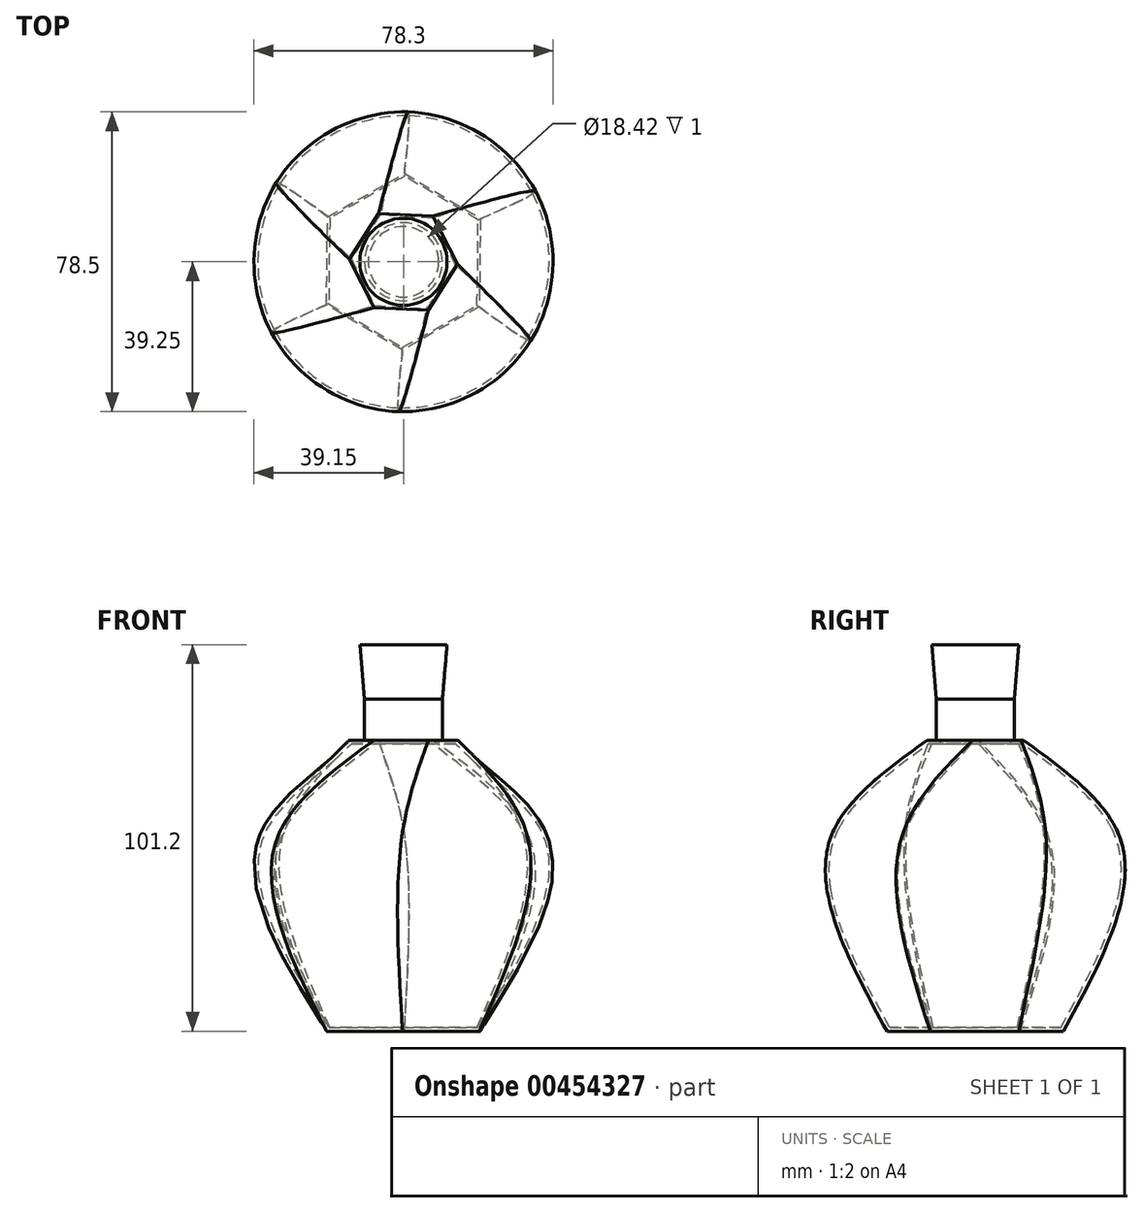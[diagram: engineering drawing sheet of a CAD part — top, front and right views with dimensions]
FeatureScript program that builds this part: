
annotation { "Feature Type Name" : "Feature", "Feature Type Description" : "" }
export const myFeature = defineFeature(function(context is Context, id is Id, definition is map)
    precondition{}
    {
        {
            var Q0;
            Q0=qCreatedBy(makeId("Top.planeOp"),FACE);
            var sketch = newSketch(context, id + "F0", { "sketchPlane" : qUnion([Q0])});
            skCircle(sketch, "E0.cCircle", {"center": v(0, 0) * mm, "radius": 23.1 * mm, "construction": true});
            skLineSegment(sketch, "E0.0", {"start": v(-20.14, -11.32) * mm, "end": v(-19.88, 11.78) * mm});
            skLineSegment(sketch, "E0.1", {"start": v(-19.88, 11.78) * mm, "end": v(0.27, 23.1) * mm});
            skLineSegment(sketch, "E0.2", {"start": v(0.27, 23.1) * mm, "end": v(20.14, 11.32) * mm});
            skLineSegment(sketch, "E0.3", {"start": v(20.14, 11.32) * mm, "end": v(19.88, -11.78) * mm});
            skLineSegment(sketch, "E0.4", {"start": v(19.88, -11.78) * mm, "end": v(-0.27, -23.1) * mm});
            skLineSegment(sketch, "E0.5", {"start": v(-0.27, -23.1) * mm, "end": v(-20.14, -11.32) * mm});
            skSolve(sketch);
        }
        {
            var Q0;
            Q0=qCreatedBy(makeId("Top.planeOp"),FACE);
            cPlane(context, id + "F1", {"entities" : qUnion([Q0]), "cplaneType" : CPlaneType.OFFSET, "offset" : 50.8 * mm, "width" : 152.4 * mm, "height" : 152.4 * mm});
        }
        {
            var Q0;
            Q0=qCreatedBy(id+"F1.planeOp",FACE);
            var sketch = newSketch(context, id + "F2", { "sketchPlane" : qUnion([Q0])});
            skCircle(sketch, "E1", {"center": v(0, 0) * mm, "radius": 37.82 * mm});
            skSolve(sketch);
        }
        {
            var Q0;
            Q0=qCreatedBy(id+"F1.planeOp",FACE);
            cPlane(context, id + "F3", {"entities" : qUnion([Q0]), "cplaneType" : CPlaneType.OFFSET, "offset" : 38.1 * mm, "width" : 152.4 * mm, "height" : 152.4 * mm});
        }
        {
            var Q0;
            Q0=qCreatedBy(id+"F1.planeOp",FACE);
            cPlane(context, id + "F4", {"entities" : qUnion([Q0]), "cplaneType" : CPlaneType.OFFSET, "offset" : 25.4 * mm, "width" : 152.4 * mm, "height" : 152.4 * mm});
        }
        {
            var Q0;
            Q0=qCreatedBy(id+"F4.planeOp",FACE);
            var sketch = newSketch(context, id + "F5", { "sketchPlane" : qUnion([Q0])});
            skCircle(sketch, "E2.cCircle", {"center": v(0, 0) * mm, "radius": 14.22 * mm, "construction": true});
            skLineSegment(sketch, "E2.0", {"start": v(6.55, -12.63) * mm, "end": v(-7.66, -11.98) * mm});
            skLineSegment(sketch, "E2.1", {"start": v(-7.66, -11.98) * mm, "end": v(-14.2, 0.64) * mm});
            skLineSegment(sketch, "E2.2", {"start": v(-14.2, 0.64) * mm, "end": v(-6.55, 12.63) * mm});
            skLineSegment(sketch, "E2.3", {"start": v(-6.55, 12.63) * mm, "end": v(7.66, 11.98) * mm});
            skLineSegment(sketch, "E2.4", {"start": v(7.66, 11.98) * mm, "end": v(14.2, -0.64) * mm});
            skLineSegment(sketch, "E2.5", {"start": v(14.2, -0.64) * mm, "end": v(6.55, -12.63) * mm});
            skSolve(sketch);
        }
        {
            var Q0;
            Q0=makeQuery(id+"F0.imprint","IMPRINT",FACE,{"disambiguationData":[TD([[makeQuery(id+"F0.imprint","IMPRINT",EDGE,{"derivedFrom":sQuery(id+"F0.wireOp",EDGE,"E0.0")}),-1.0]])]});
            var Q1;
            Q1=makeQuery(id+"F2.imprint","IMPRINT",FACE,{"disambiguationData":[TD([[makeQuery(id+"F2.imprint","IMPRINT",EDGE,{"derivedFrom":sQuery(id+"F2.wireOp",EDGE,"E1")}),1.0]])]});
            var Q2;
            Q2=makeQuery(id+"F5.imprint","IMPRINT",FACE,{"disambiguationData":[TD([[makeQuery(id+"F5.imprint","IMPRINT",EDGE,{"derivedFrom":sQuery(id+"F5.wireOp",EDGE,"E2.0")}),-1.0]])]});
            loft(context, id + "F6", {"sheetProfilesArray" : [{ "sheetProfileEntities" : qUnion([Q0]) }, { "sheetProfileEntities" : qUnion([Q1]) }, { "sheetProfileEntities" : qUnion([Q2]) }]});
        }
        {
            var Q0;
            Q0=makeQuery(id+"F6.opLoft","CAP_FACE",FACE,{"disambiguationData":[OSD([makeQuery(id+"F5.imprint","IMPRINT",FACE,{"disambiguationData":[TD([[makeQuery(id+"F5.imprint","IMPRINT",EDGE,{"derivedFrom":sQuery(id+"F5.wireOp",EDGE,"E2.0")}),-1.0]])]})])],"isStart":true});
            var sketch = newSketch(context, id + "F7", { "sketchPlane" : qUnion([Q0])});
            skCircle(sketch, "E3", {"center": v(0, 0) * mm, "radius": 10.2 * mm});
            skSolve(sketch);
        }
        {
            var Q0;
            Q0=makeQuery(id+"F7.imprint","IMPRINT",FACE,{"disambiguationData":[TD([[makeQuery(id+"F7.imprint","IMPRINT",EDGE,{"derivedFrom":sQuery(id+"F7.wireOp",EDGE,"E3")}),1.0]])]});
            extrude(context, id + "F8", {"entities" : qUnion([Q0]), "operationType" : NewBodyOperationType.ADD, "depth" : 20.57 * mm});
        }
        {
            var Q0;
            Q0=makeQuery(id+"F8.opExtrude","CAP_FACE",FACE,{"disambiguationData":[OSD([sQuery(id+"F7.wireOp",EDGE,"E3")])],"isStart":false});
            shell(context, id + "F9", {"entities" : qUnion([Q0]), "thickness" : 1 * mm});
        }
        {
            var Q0;
            Q0=qCreatedBy(makeId("Front.planeOp"),FACE);
            var sketch = newSketch(context, id + "F10", { "sketchPlane" : qUnion([Q0])});
            skCircle(sketch, "E4", {"center": v(0, 93.98) * mm, "radius": 1.73 * mm});
            skSolve(sketch);
        }
        {
            var Q0;
            Q0=qCreatedBy(id+"F4.planeOp",FACE);
            cPlane(context, id + "F11", {"entities" : qUnion([Q0]), "cplaneType" : CPlaneType.OFFSET, "offset" : 25 * mm, "width" : 150 * mm, "height" : 150 * mm});
        }
        {
            var Q0;
            Q0=sQuery(id+"F10.wireOp",EDGE,"E4");
            extrude(context, id + "F12", {"bodyType" : ToolBodyType.SURFACE, "surfaceEntities" : qUnion([Q0]), "oppositeDirection" : true, "depth" : 12.5 * mm});
        }
        {
            var Q0;
            Q0=qCreatedBy(id+"F4.planeOp",FACE);
            var sketch = newSketch(context, id + "F13", { "sketchPlane" : qUnion([Q0])});
            skCircle(sketch, "E5", {"center": v(0, 0) * mm, "radius": 9.3 * mm});
            skSolve(sketch);
        }
        {
            var Q0;
            Q0=qCreatedBy(id+"F11.planeOp",FACE);
            var sketch = newSketch(context, id + "F14", { "sketchPlane" : qUnion([Q0])});
            skCircle(sketch, "E6", {"center": v(0, 0) * mm, "radius": 11.41 * mm});
            skSolve(sketch);
        }
        {
            var Q1;
            Q1 = qSketchRegion(id + "F13", true);
            var Q2;
            Q2 = qSketchRegion(id + "F14", true);
            loft(context, id + "F15", {"operationType" : NewBodyOperationType.ADD, "sheetProfilesArray" : [{ "sheetProfileEntities" : qUnion([Q1]) }, { "sheetProfileEntities" : qUnion([Q2]) }]});
        }
    });
